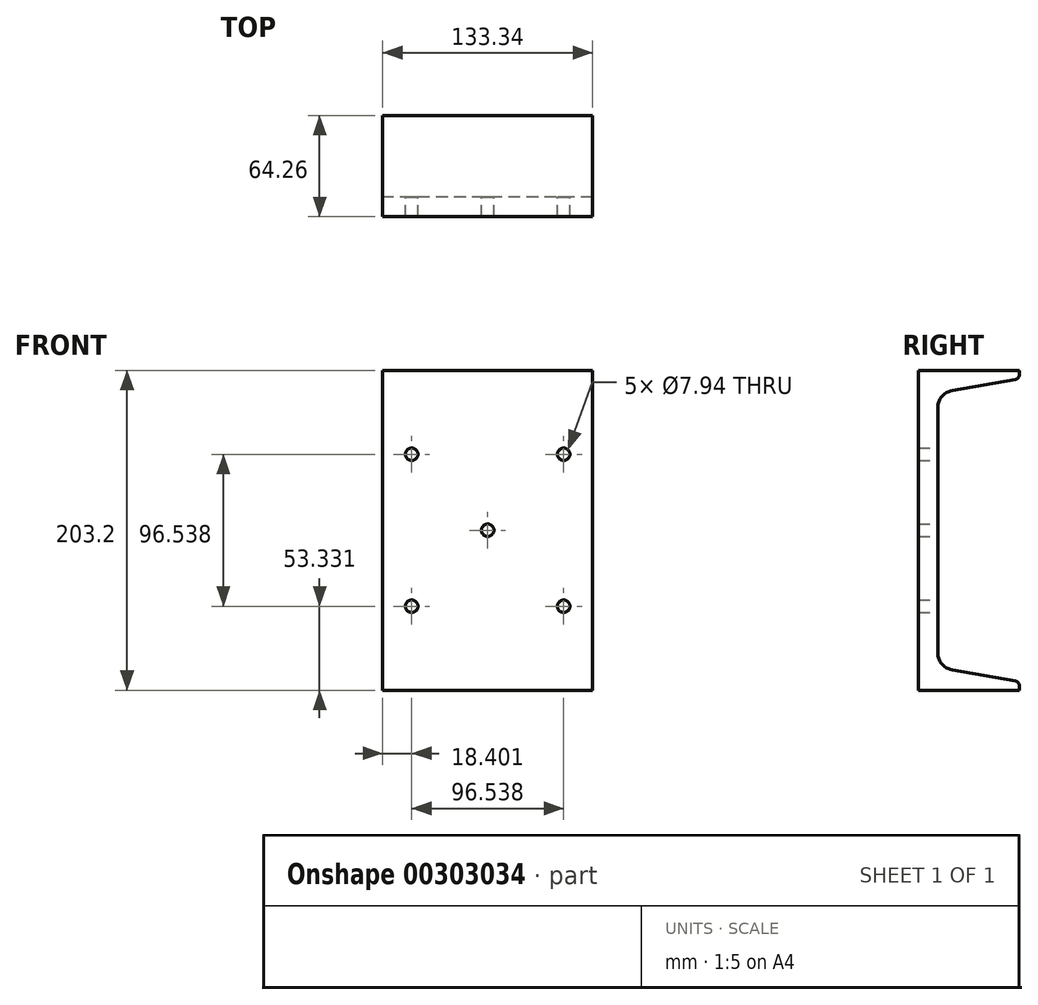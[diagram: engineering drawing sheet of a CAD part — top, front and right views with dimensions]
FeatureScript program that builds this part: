
annotation { "Feature Type Name" : "Feature", "Feature Type Description" : "" }
export const myFeature = defineFeature(function(context is Context, id is Id, definition is map)
    precondition{}
    {
        {
            var Q0;
            Q0=qCreatedBy(makeId("Right.planeOp"),FACE);
            var sketch = newSketch(context, id + "F0", { "sketchPlane" : qUnion([Q0])});
            skLineSegment(sketch, "E0", {"start": v(64.26, 101.6) * mm, "end": v(64.26, 98.93) * mm});
            skArc(sketch, "E1", {"start": v(64.26, 98.93) * mm, "mid": v(63.52, 96.9) * mm, "end": v(61.64, 95.8) * mm});
            skLineSegment(sketch, "E2", {"start": v(61.64, 95.8) * mm, "end": v(21.56, 88.74) * mm});
            skArc(sketch, "E3", {"start": v(21.56, 88.74) * mm, "mid": v(14.97, 84.94) * mm, "end": v(12.37, 77.79) * mm});
            skLineSegment(sketch, "E4", {"start": v(12.37, 77.79) * mm, "end": v(12.37, -77.79) * mm});
            skArc(sketch, "E5", {"start": v(12.37, -77.79) * mm, "mid": v(14.97, -84.94) * mm, "end": v(21.56, -88.74) * mm});
            skLineSegment(sketch, "E6", {"start": v(21.56, -88.74) * mm, "end": v(61.64, -95.8) * mm});
            skArc(sketch, "E7", {"start": v(61.64, -95.8) * mm, "mid": v(63.52, -96.9) * mm, "end": v(64.26, -98.93) * mm});
            skLineSegment(sketch, "E8", {"start": v(64.26, -98.93) * mm, "end": v(64.26, -101.6) * mm});
            skLineSegment(sketch, "E9", {"start": v(64.26, -101.6) * mm, "end": v(0, -101.6) * mm});
            skLineSegment(sketch, "E10", {"start": v(0, -101.6) * mm, "end": v(0, 101.6) * mm});
            skLineSegment(sketch, "E11", {"start": v(0, 101.6) * mm, "end": v(64.26, 101.6) * mm});
            skSolve(sketch);
        }
        {
            var Q0;
            Q0=makeQuery(id+"F0.imprint","IMPRINT",FACE,{"disambiguationData":[TD([[makeQuery(id+"F0.imprint","IMPRINT",EDGE,{"derivedFrom":sQuery(id+"F0.wireOp",EDGE,"E0")}),-1.0]])]});
            extrude(context, id + "F1", {"entities" : qUnion([Q0]), "depth" : 133.35 * mm, "symmetric" : true});
        }
        {
            var Q0;
            Q0=qCreatedBy(makeId("Front.planeOp"),FACE);
            var sketch = newSketch(context, id + "F2", { "sketchPlane" : qUnion([Q0])});
            skCircle(sketch, "E12", {"center": v(0, 0) * mm, "radius": 68.26 * mm, "construction": true});
            skPoint(sketch, "E13", {"position": v(-48.27, 48.27) * mm});
            skPoint(sketch, "E14", {"position": v(48.27, 48.27) * mm});
            skPoint(sketch, "E15", {"position": v(48.27, -48.27) * mm});
            skPoint(sketch, "E16", {"position": v(-48.27, -48.27) * mm});
            skLineSegment(sketch, "E17", {"start": v(0, 0) * mm, "end": v(-48.27, 48.27) * mm, "construction": true});
            skSolve(sketch);
        }
        {
            var Q0;
            Q0=sQuery(id+"F2.wireOp",VERTEX,"E13");
            var Q1;
            Q1=sQuery(id+"F2.wireOp",VERTEX,"E14");
            var Q2;
            Q2=sQuery(id+"F2.wireOp",VERTEX,"E15");
            var Q3;
            Q3=sQuery(id+"F2.wireOp",VERTEX,"E16");
            var Q4;
            Q4=sQuery(id+"F2.wireOp",VERTEX,"E12.center");
            var Q5;
            Q5=makeQuery(id+"F1.opExtrude","SWEPT_BODY",BODY,{"disambiguationData":[OSD([sQuery(id+"F0.wireOp",EDGE,"E0"),sQuery(id+"F0.wireOp",EDGE,"E1"),sQuery(id+"F0.wireOp",EDGE,"E2"),sQuery(id+"F0.wireOp",EDGE,"E3"),sQuery(id+"F0.wireOp",EDGE,"E4"),sQuery(id+"F0.wireOp",EDGE,"E5"),sQuery(id+"F0.wireOp",EDGE,"E6"),sQuery(id+"F0.wireOp",EDGE,"E7"),sQuery(id+"F0.wireOp",EDGE,"E8"),sQuery(id+"F0.wireOp",EDGE,"E9"),sQuery(id+"F0.wireOp",EDGE,"E10"),sQuery(id+"F0.wireOp",EDGE,"E11")])]});
            hole(context, id + "F3", {"style" : HoleStyle.SIMPLE, "endStyle" : HoleEndStyle.BLIND, "standardTappedOrClearance" : lookupTablePath({ "standard" : "ANSI", "engagement" : "75%", "pitch" : "16 tpi", "size" : "3/8", "type" : "Tapped" }), "standardBlindInLast" : lookupTablePath({ "standard" : "ANSI", "engagement" : "75%", "pitch" : "16 tpi", "size" : "3/8", "type" : "Tapped" }), "holeDiameter" : 7.94 * mm, "showTappedDepth" : true, "holeDepth" : 17.46 * mm, "tappedDepth" : 12.7 * mm, "tapClearance" : 3, "locations" : qUnion([Q0, Q1, Q2, Q3, Q4]), "scope" : qUnion([Q5]), "majorDiameter" : 9.53 * mm});
        }
    });
